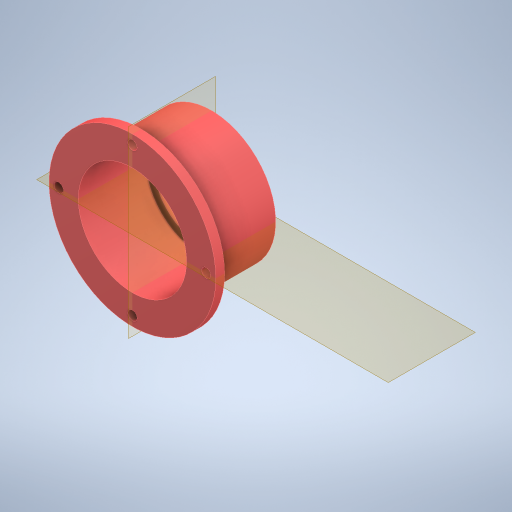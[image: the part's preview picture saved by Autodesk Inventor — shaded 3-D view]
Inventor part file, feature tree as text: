
AUTODESK INVENTOR PART (.ipt)
format: ipt  version: 2024.3 (Build 283343000, 343)  size: 279,040 bytes
history: native  units: in
note: dims shown in document units (in); Inventor stores cm internally (conversion verified against a paired STEP export)
features: plane x1, imported_body x1
ambient origin geometry x8: Origin, YZ Plane, XZ Plane, XY Plane, X Axis, Y Axis, Z Axis, Center Point
bodies: Solid1 (feature_tree)
feature tree (2):
  plane  "Work Plane1"
  imported_body  "Base1"
